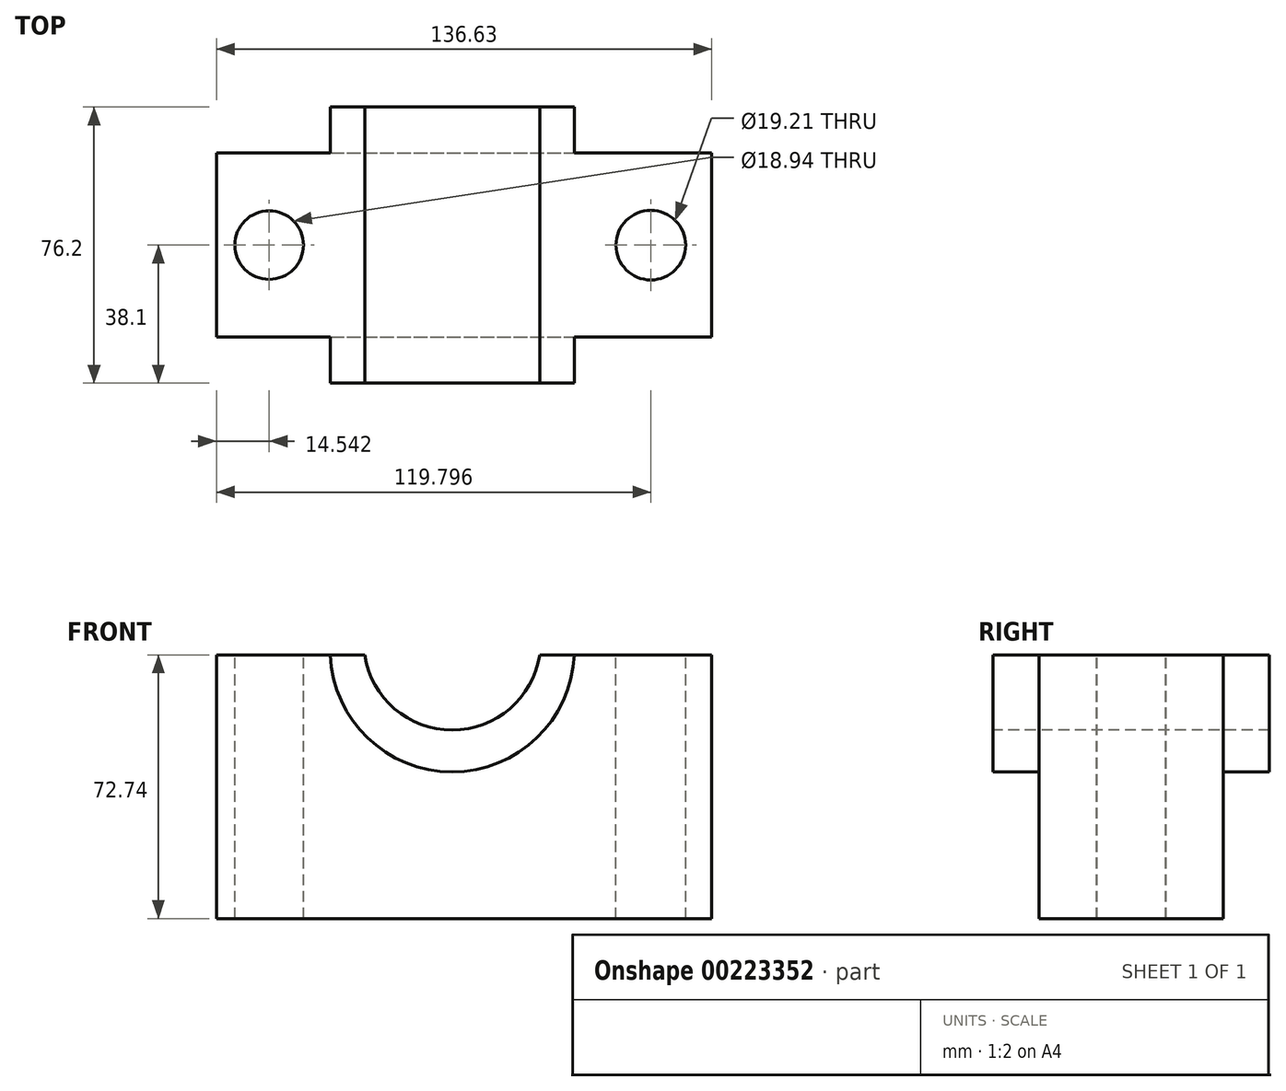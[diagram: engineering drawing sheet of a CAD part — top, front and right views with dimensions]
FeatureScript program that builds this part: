
annotation { "Feature Type Name" : "Feature", "Feature Type Description" : "" }
export const myFeature = defineFeature(function(context is Context, id is Id, definition is map)
    precondition{}
    {
        {
            var Q0;
            Q0=qCreatedBy(makeId("Front.planeOp"),FACE);
            var sketch = newSketch(context, id + "F0", { "sketchPlane" : qUnion([Q0])});
            skLineSegment(sketch, "E0.bottom", {"start": v(-65.03, 60.9) * mm, "end": v(71.6, 60.9) * mm});
            skLineSegment(sketch, "E0.top", {"start": v(-65.03, -56.62) * mm, "end": v(71.6, -56.62) * mm});
            skLineSegment(sketch, "E0.left", {"start": v(-65.03, 60.9) * mm, "end": v(-65.03, -56.62) * mm});
            skLineSegment(sketch, "E0.right", {"start": v(71.6, 60.9) * mm, "end": v(71.6, -56.62) * mm});
            skSolve(sketch);
        }
        {
            var Q0;
            Q0 = qSketchRegion(id + "F0", true);
            extrude(context, id + "F1", {"entities" : qUnion([Q0]), "depth" : 25.4 * mm, "hasSecondDirection" : true, "secondDirectionOppositeDirection" : true, "secondDirectionDepth" : 25.4 * mm});
        }
        {
            var Q0;
            Q0=qCreatedBy(makeId("Front.planeOp"),FACE);
            var sketch = newSketch(context, id + "F2", { "sketchPlane" : qUnion([Q0])});
            skCircle(sketch, "E1", {"center": v(0, 17.54) * mm, "radius": 33.68 * mm});
            skSolve(sketch);
        }
        {
            var Q0;
            Q0 = qSketchRegion(id + "F2", true);
            extrude(context, id + "F3", {"entities" : qUnion([Q0]), "operationType" : NewBodyOperationType.ADD, "depth" : 38.1 * mm, "hasSecondDirection" : true, "secondDirectionOppositeDirection" : true, "secondDirectionDepth" : 38.1 * mm});
        }
        {
            var Q0;
            Q0=qCreatedBy(makeId("Front.planeOp"),FACE);
            var sketch = newSketch(context, id + "F4", { "sketchPlane" : qUnion([Q0])});
            skCircle(sketch, "E2", {"center": v(0, 19.82) * mm, "radius": 24.43 * mm});
            skSolve(sketch);
        }
        {
            var Q0;
            Q0 = qSketchRegion(id + "F4", true);
            extrude(context, id + "F5", {"entities" : qUnion([Q0]), "operationType" : NewBodyOperationType.REMOVE, "endBound" : BoundingType.THROUGH_ALL, "oppositeDirection" : true, "depth" : 25.4 * mm, "hasSecondDirection" : true, "secondDirectionBound" : SecondDirectionBoundingType.THROUGH_ALL, "secondDirectionOppositeDirection" : false, "secondDirectionDepth" : 25.4 * mm});
        }
        {
            var Q0;
            Q0=qCreatedBy(makeId("Front.planeOp"),FACE);
            var sketch = newSketch(context, id + "F6", { "sketchPlane" : qUnion([Q0])});
            skLineSegment(sketch, "E3.bottom", {"start": v(-75.87, 16.12) * mm, "end": v(75.87, 16.12) * mm});
            skLineSegment(sketch, "E3.top", {"start": v(-75.87, 65.46) * mm, "end": v(75.87, 65.46) * mm});
            skLineSegment(sketch, "E3.left", {"start": v(-75.87, 16.12) * mm, "end": v(-75.87, 65.46) * mm});
            skLineSegment(sketch, "E3.right", {"start": v(75.87, 16.12) * mm, "end": v(75.87, 65.46) * mm});
            skSolve(sketch);
        }
        {
            var Q0;
            Q0 = qSketchRegion(id + "F6", true);
            extrude(context, id + "F7", {"entities" : qUnion([Q0]), "operationType" : NewBodyOperationType.REMOVE, "endBound" : BoundingType.THROUGH_ALL, "oppositeDirection" : true, "depth" : 25.4 * mm, "hasSecondDirection" : true, "secondDirectionBound" : SecondDirectionBoundingType.THROUGH_ALL, "secondDirectionOppositeDirection" : false, "secondDirectionDepth" : 25.4 * mm});
        }
        {
            var Q0;
            Q0=qCreatedBy(makeId("Top.planeOp"),FACE);
            var sketch = newSketch(context, id + "F8", { "sketchPlane" : qUnion([Q0])});
            skCircle(sketch, "E4", {"center": v(-50.49, 0) * mm, "radius": 9.47 * mm});
            skCircle(sketch, "E5", {"center": v(54.77, 0) * mm, "radius": 9.6 * mm});
            skSolve(sketch);
        }
        {
            var Q0;
            Q0 = qSketchRegion(id + "F8", true);
            extrude(context, id + "F9", {"entities" : qUnion([Q0]), "operationType" : NewBodyOperationType.REMOVE, "endBound" : BoundingType.THROUGH_ALL, "oppositeDirection" : true, "depth" : 25.4 * mm, "hasSecondDirection" : true, "secondDirectionBound" : SecondDirectionBoundingType.THROUGH_ALL, "secondDirectionOppositeDirection" : false, "secondDirectionDepth" : 25.4 * mm});
        }
    });
